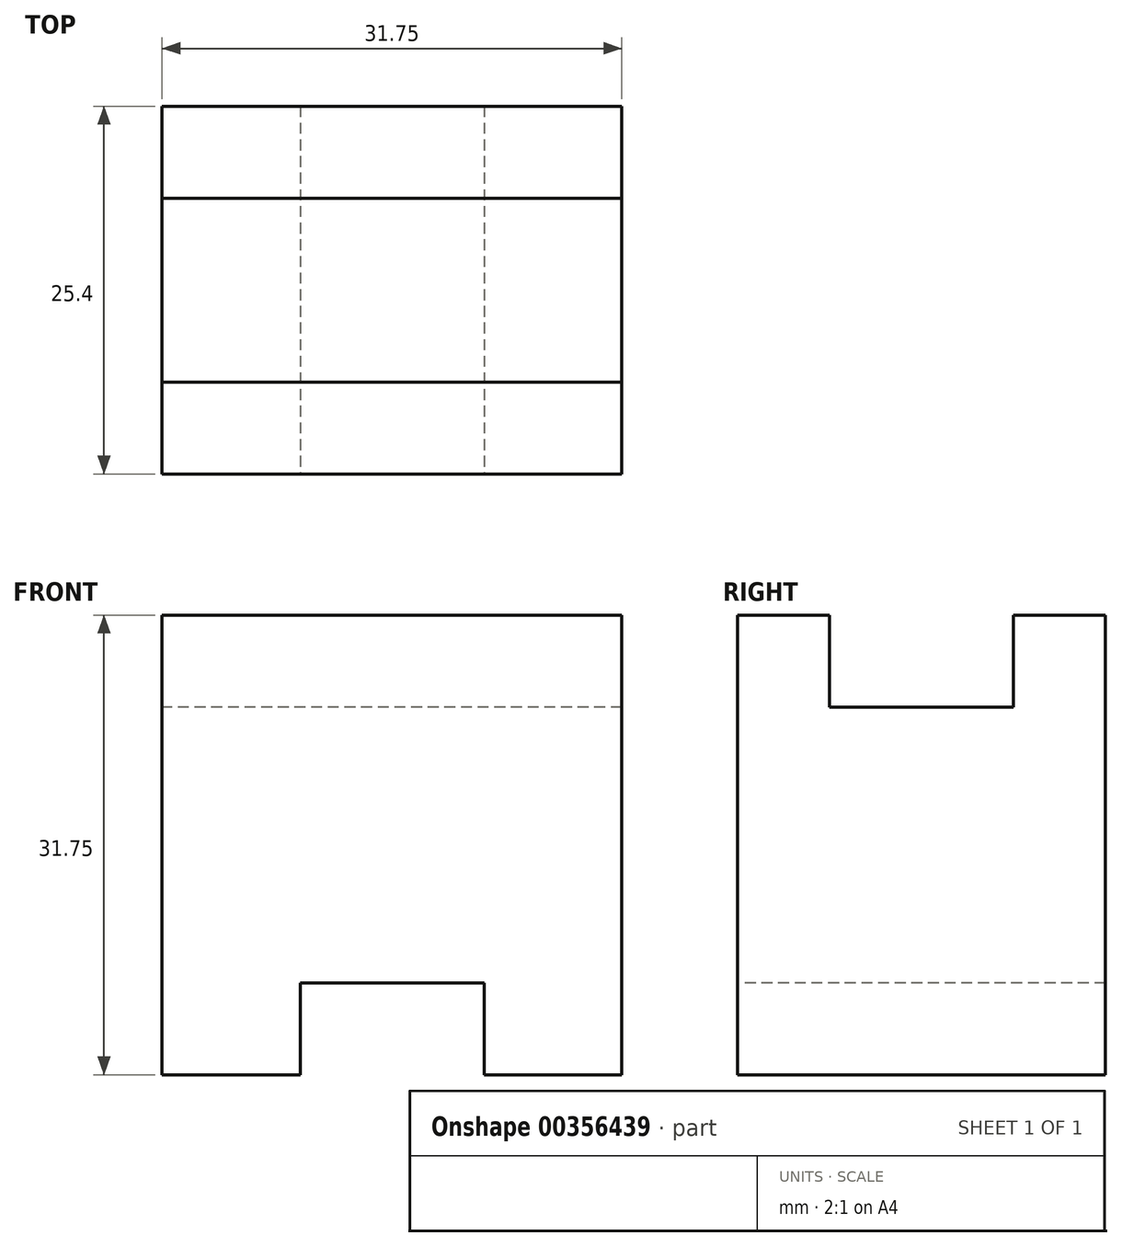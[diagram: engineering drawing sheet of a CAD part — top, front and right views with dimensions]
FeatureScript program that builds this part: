
annotation { "Feature Type Name" : "Feature", "Feature Type Description" : "" }
export const myFeature = defineFeature(function(context is Context, id is Id, definition is map)
    precondition{}
    {
        {
            var Q0;
            Q0=qCreatedBy(makeId("Right.planeOp"),FACE);
            var sketch = newSketch(context, id + "F0", { "sketchPlane" : qUnion([Q0])});
            skLineSegment(sketch, "E0", {"start": v(0, 0) * mm, "end": v(25.4, 0) * mm});
            skLineSegment(sketch, "E1", {"start": v(25.4, 0) * mm, "end": v(25.4, 31.75) * mm});
            skLineSegment(sketch, "E2", {"start": v(25.4, 31.75) * mm, "end": v(19.05, 31.75) * mm});
            skLineSegment(sketch, "E3", {"start": v(19.05, 31.75) * mm, "end": v(19.05, 25.4) * mm});
            skLineSegment(sketch, "E4", {"start": v(19.05, 25.4) * mm, "end": v(6.35, 25.4) * mm});
            skLineSegment(sketch, "E5", {"start": v(6.35, 25.4) * mm, "end": v(6.35, 31.75) * mm});
            skLineSegment(sketch, "E6", {"start": v(6.35, 31.75) * mm, "end": v(0, 31.75) * mm});
            skLineSegment(sketch, "E7", {"start": v(0, 31.75) * mm, "end": v(0, 0) * mm});
            skSolve(sketch);
        }
        {
            var Q0;
            Q0 = qSketchRegion(id + "F0", true);
            extrude(context, id + "F1", {"entities" : qUnion([Q0]), "depth" : 31.75 * mm});
        }
        {
            var Q0;
            Q0=makeQuery(id+"F1.opExtrude","SWEPT_FACE",FACE,{"disambiguationData":[OSD([sQuery(id+"F0.wireOp",EDGE,"E7")])]});
            var sketch = newSketch(context, id + "F2", { "sketchPlane" : qUnion([Q0])});
            skLineSegment(sketch, "E8", {"start": v(9.54, 0) * mm, "end": v(9.54, 6.35) * mm});
            skLineSegment(sketch, "E9", {"start": v(9.54, 6.35) * mm, "end": v(22.24, 6.35) * mm});
            skLineSegment(sketch, "E10", {"start": v(22.24, 6.35) * mm, "end": v(22.24, 0) * mm});
            skLineSegment(sketch, "E11", {"start": v(22.24, 0) * mm, "end": v(9.54, 0) * mm});
            skLineSegment(sketch, "E12", {"start": v(9.54, 0) * mm, "end": v(22.24, 0) * mm});
            skSolve(sketch);
        }
        {
            var Q0;
            Q0 = qSketchRegion(id + "F2", true);
            extrude(context, id + "F3", {"entities" : qUnion([Q0]), "operationType" : NewBodyOperationType.REMOVE, "oppositeDirection" : true, "depth" : 25.4 * mm});
        }
    });
